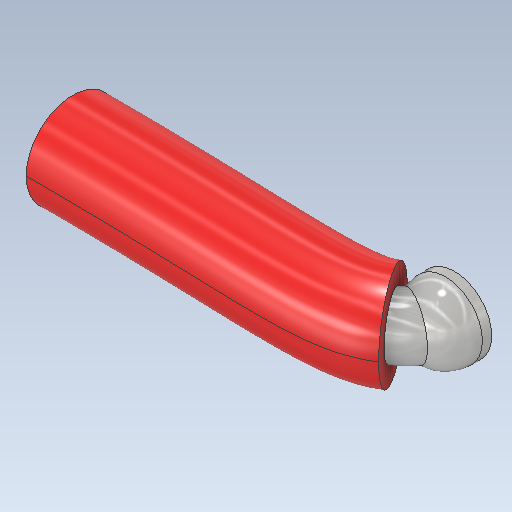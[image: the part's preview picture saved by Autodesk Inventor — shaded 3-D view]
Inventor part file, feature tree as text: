
AUTODESK INVENTOR PART (.ipt)
format: ipt  version: 2020.1 (Build 241239000, 239)  size: 270,848 bytes
history: native  units: mm
features: sketch x5, sweep x2, extrude x1, fillet x1, plane x1
ambient origin geometry x8: Origin, YZ Plane, XZ Plane, XY Plane, X Axis, Y Axis, Z Axis, Center Point
bodies: Solid1 (feature_tree)
feature tree (10):
  extrude  "Extrusion1"  Depth=2.5mm TaperAngle=0.0deg
  fillet  "Fillet1"  Radius=2.0mm
  sweep  "Sweep1"
  plane  "Work Plane1"
  sweep  "Sweep4"
  sketch  "Sketch1"  dims[d0=4.0mm d1=2.5mm d2=0.0mm d3=2.0mm]
  sketch  "Sketch2"  dims[d4=2.6mm d5=3.06mm]
  sketch  "Sketch3"  dims[d6=0.0mm d7=0.0mm d9=5.0mm]
  sketch  "Sketch4"  dims[d18=4.0mm d19=-2.0mm d20=0.0mm d21=0.0mm]
  sketch  "3D Sketch1"
